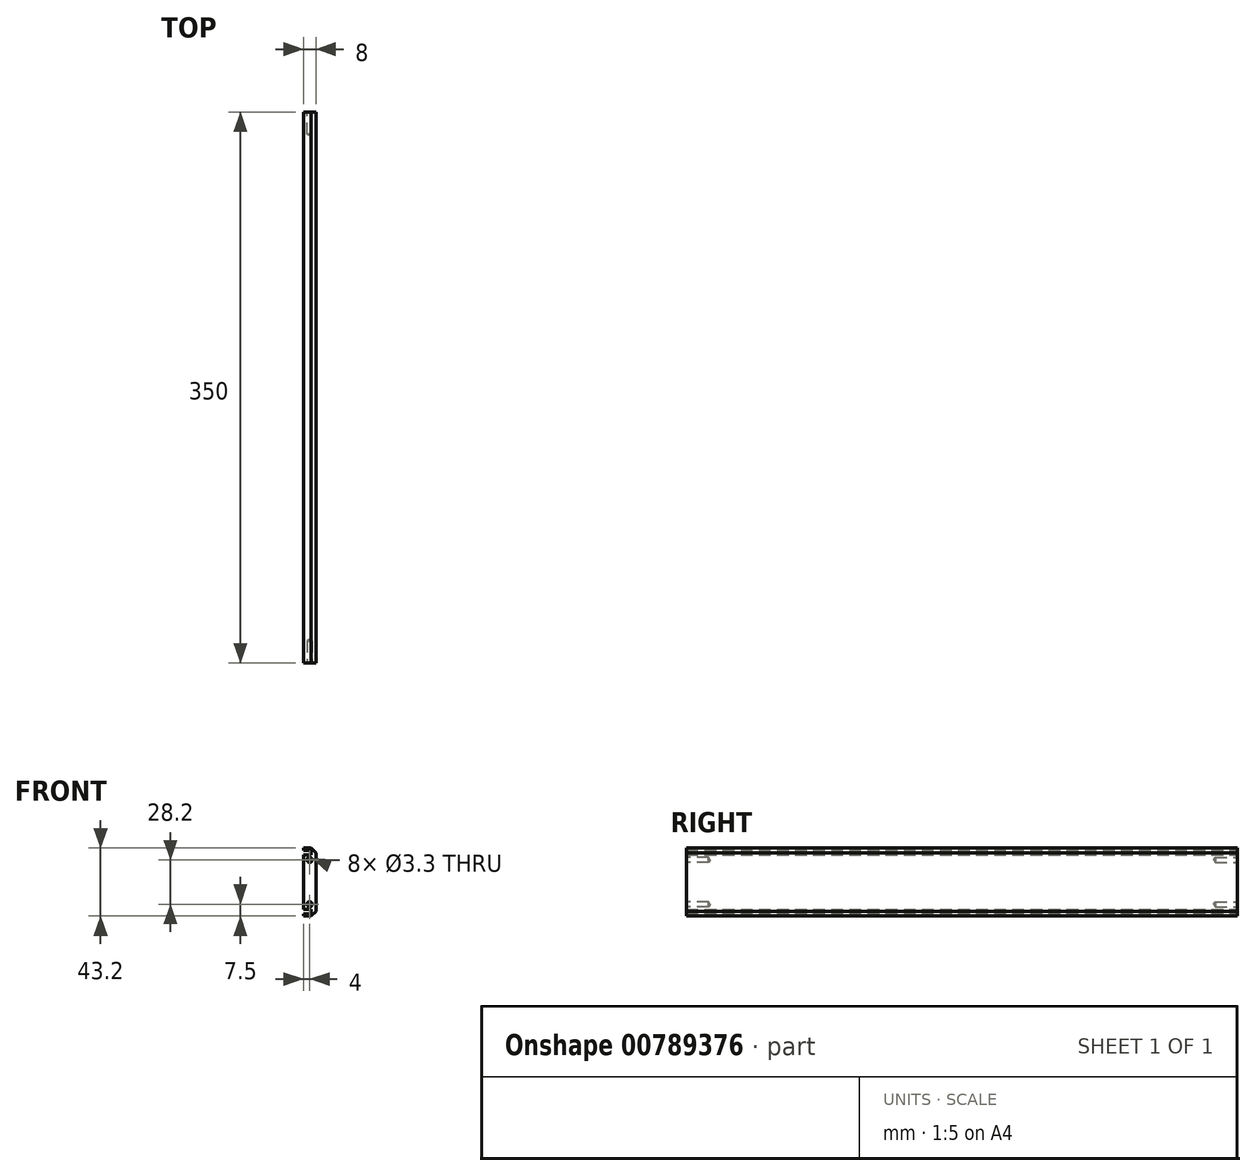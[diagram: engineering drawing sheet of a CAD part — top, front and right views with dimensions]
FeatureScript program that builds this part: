
annotation { "Feature Type Name" : "Feature", "Feature Type Description" : "" }
export const myFeature = defineFeature(function(context is Context, id is Id, definition is map)
    precondition{}
    {
        {
            var Q0;
            Q0=qCreatedBy(makeId("Front.planeOp"),FACE);
            var sketch = newSketch(context, id + "F0", { "sketchPlane" : qUnion([Q0])});
            skLineSegment(sketch, "E0", {"start": v(0, 29.5) * mm, "end": v(5, 29.5) * mm});
            skLineSegment(sketch, "E1", {"start": v(5, 29.5) * mm, "end": v(5, 32.5) * mm});
            skLineSegment(sketch, "E2", {"start": v(5, 32.5) * mm, "end": v(0, 32.5) * mm});
            skLineSegment(sketch, "E3", {"start": v(0, 32.5) * mm, "end": v(0, 33.85) * mm});
            skLineSegment(sketch, "E4", {"start": v(0, 33.85) * mm, "end": v(8, 33.85) * mm});
            skLineSegment(sketch, "E5", {"start": v(8, 33.85) * mm, "end": v(8, -9.35) * mm});
            skLineSegment(sketch, "E6", {"start": v(8, -9.35) * mm, "end": v(0, -9.35) * mm});
            skLineSegment(sketch, "E7", {"start": v(0, -9.35) * mm, "end": v(0, -8) * mm});
            skLineSegment(sketch, "E8", {"start": v(0, -8) * mm, "end": v(5, -8) * mm});
            skLineSegment(sketch, "E9", {"start": v(5, -8) * mm, "end": v(5, -5) * mm});
            skLineSegment(sketch, "E10", {"start": v(5, -5) * mm, "end": v(0, -5) * mm});
            skLineSegment(sketch, "E11", {"start": v(0, -5) * mm, "end": v(0, 29.5) * mm});
            skSolve(sketch);
        }
        {
            var Q0;
            Q0 = qSketchRegion(id + "F0", true);
            extrude(context, id + "F1", {"entities" : qUnion([Q0]), "depth" : 350 * mm, "offsetDistance" : 25 * mm});
        }
        {
            var Q0;
            Q0=makeQuery(id+"F1.opExtrude","SWEPT_EDGE",EDGE,{"disambiguationData":[OSD([sQuery(id+"F0.wireOp",EDGE,"E4"),sQuery(id+"F0.wireOp",EDGE,"E5")])]});
            var Q1;
            Q1=makeQuery(id+"F1.opExtrude","SWEPT_EDGE",EDGE,{"disambiguationData":[OSD([sQuery(id+"F0.wireOp",EDGE,"E5"),sQuery(id+"F0.wireOp",EDGE,"E6")])]});
            chamfer(context, id + "F2", {"entities" : qUnion([Q0, Q1]), "width" : 3 * mm, "tangentPropagation" : true});
        }
        {
            var Q0;
            Q0=makeQuery(id+"F1.opExtrude","CAP_FACE",FACE,{"disambiguationData":[OSD([sQuery(id+"F0.wireOp",EDGE,"E0"),sQuery(id+"F0.wireOp",EDGE,"E1"),sQuery(id+"F0.wireOp",EDGE,"E2"),sQuery(id+"F0.wireOp",EDGE,"E3"),sQuery(id+"F0.wireOp",EDGE,"E4"),sQuery(id+"F0.wireOp",EDGE,"E5"),sQuery(id+"F0.wireOp",EDGE,"E6"),sQuery(id+"F0.wireOp",EDGE,"E7"),sQuery(id+"F0.wireOp",EDGE,"E8"),sQuery(id+"F0.wireOp",EDGE,"E9"),sQuery(id+"F0.wireOp",EDGE,"E10"),sQuery(id+"F0.wireOp",EDGE,"E11")])],"isStart":false});
            var sketch = newSketch(context, id + "F3", { "sketchPlane" : qUnion([Q0])});
            skPoint(sketch, "E12", {"position": v(4, 26.35) * mm});
            skPoint(sketch, "E13", {"position": v(4, -1.85) * mm});
            skSolve(sketch);
        }
        {
            var Q0;
            Q0=sQuery(id+"F3.wireOp",VERTEX,"E12");
            var Q1;
            Q1=sQuery(id+"F3.wireOp",VERTEX,"E13");
            var Q2;
            Q2=makeQuery(id+"F1.opExtrude","SWEPT_BODY",BODY,{"disambiguationData":[OSD([sQuery(id+"F0.wireOp",EDGE,"E0"),sQuery(id+"F0.wireOp",EDGE,"E1"),sQuery(id+"F0.wireOp",EDGE,"E2"),sQuery(id+"F0.wireOp",EDGE,"E3"),sQuery(id+"F0.wireOp",EDGE,"E4"),sQuery(id+"F0.wireOp",EDGE,"E5"),sQuery(id+"F0.wireOp",EDGE,"E6"),sQuery(id+"F0.wireOp",EDGE,"E7"),sQuery(id+"F0.wireOp",EDGE,"E8"),sQuery(id+"F0.wireOp",EDGE,"E9"),sQuery(id+"F0.wireOp",EDGE,"E10"),sQuery(id+"F0.wireOp",EDGE,"E11")])]});
            hole(context, id + "F4", {"style" : HoleStyle.SIMPLE, "endStyle" : HoleEndStyle.BLIND, "standardTappedOrClearance" : lookupTablePath({ "standard" : "ISO", "engagement" : "75%", "pitch" : "0.7 mm", "size" : "M4", "type" : "Tapped" }), "standardBlindInLast" : lookupTablePath({ "standard" : "ISO", "engagement" : "75%", "pitch" : "0.7 mm", "size" : "M4", "type" : "Tapped" }), "holeDiameter" : 3.3 * mm, "majorDiameter" : 4 * mm, "showTappedDepth" : true, "holeDepth" : 14.1 * mm, "isTappedThrough" : true, "tappedDepth" : 12 * mm, "tapClearance" : 3, "locations" : qUnion([Q0, Q1]), "scope" : qUnion([Q2])});
        }
        {
            var Q0;
            Q0=makeQuery(id+"F1.opExtrude","CAP_FACE",FACE,{"disambiguationData":[OSD([sQuery(id+"F0.wireOp",EDGE,"E0"),sQuery(id+"F0.wireOp",EDGE,"E1"),sQuery(id+"F0.wireOp",EDGE,"E2"),sQuery(id+"F0.wireOp",EDGE,"E3"),sQuery(id+"F0.wireOp",EDGE,"E4"),sQuery(id+"F0.wireOp",EDGE,"E5"),sQuery(id+"F0.wireOp",EDGE,"E6"),sQuery(id+"F0.wireOp",EDGE,"E7"),sQuery(id+"F0.wireOp",EDGE,"E8"),sQuery(id+"F0.wireOp",EDGE,"E9"),sQuery(id+"F0.wireOp",EDGE,"E10"),sQuery(id+"F0.wireOp",EDGE,"E11")])],"isStart":true});
            var sketch = newSketch(context, id + "F5", { "sketchPlane" : qUnion([Q0])});
            skPoint(sketch, "E14", {"position": v(-4, 26.35) * mm});
            skPoint(sketch, "E15", {"position": v(-4, -1.85) * mm});
            skSolve(sketch);
        }
        {
            var Q0;
            Q0=sQuery(id+"F5.wireOp",VERTEX,"E14");
            var Q1;
            Q1=sQuery(id+"F5.wireOp",VERTEX,"E15");
            var Q2;
            Q2=makeQuery(id+"F1.opExtrude","SWEPT_BODY",BODY,{"disambiguationData":[OSD([sQuery(id+"F0.wireOp",EDGE,"E0"),sQuery(id+"F0.wireOp",EDGE,"E1"),sQuery(id+"F0.wireOp",EDGE,"E2"),sQuery(id+"F0.wireOp",EDGE,"E3"),sQuery(id+"F0.wireOp",EDGE,"E4"),sQuery(id+"F0.wireOp",EDGE,"E5"),sQuery(id+"F0.wireOp",EDGE,"E6"),sQuery(id+"F0.wireOp",EDGE,"E7"),sQuery(id+"F0.wireOp",EDGE,"E8"),sQuery(id+"F0.wireOp",EDGE,"E9"),sQuery(id+"F0.wireOp",EDGE,"E10"),sQuery(id+"F0.wireOp",EDGE,"E11")])]});
            hole(context, id + "F6", {"style" : HoleStyle.SIMPLE, "endStyle" : HoleEndStyle.BLIND, "standardTappedOrClearance" : lookupTablePath({ "standard" : "ISO", "engagement" : "75%", "pitch" : "0.7 mm", "size" : "M4", "type" : "Tapped" }), "standardBlindInLast" : lookupTablePath({ "standard" : "ISO", "engagement" : "75%", "pitch" : "0.7 mm", "size" : "M4", "type" : "Tapped" }), "holeDiameter" : 3.3 * mm, "majorDiameter" : 4 * mm, "showTappedDepth" : true, "holeDepth" : 14.1 * mm, "isTappedThrough" : true, "tappedDepth" : 12 * mm, "tapClearance" : 3, "locations" : qUnion([Q0, Q1]), "scope" : qUnion([Q2])});
        }
        {
            var Q0;
            Q0=makeQuery(id+"F1.opExtrude","SWEPT_BODY",BODY,{"disambiguationData":[OSD([sQuery(id+"F0.wireOp",EDGE,"E0"),sQuery(id+"F0.wireOp",EDGE,"E1"),sQuery(id+"F0.wireOp",EDGE,"E2"),sQuery(id+"F0.wireOp",EDGE,"E3"),sQuery(id+"F0.wireOp",EDGE,"E4"),sQuery(id+"F0.wireOp",EDGE,"E5"),sQuery(id+"F0.wireOp",EDGE,"E6"),sQuery(id+"F0.wireOp",EDGE,"E7"),sQuery(id+"F0.wireOp",EDGE,"E8"),sQuery(id+"F0.wireOp",EDGE,"E9"),sQuery(id+"F0.wireOp",EDGE,"E10"),sQuery(id+"F0.wireOp",EDGE,"E11")])]});
            transform(context, id + "F7", {"entities" : qUnion([Q0]), "transformType" : TransformType.TRANSLATION_3D, "dx" : 0 * mm, "dy" : 0 * mm, "dz" : 0 * mm, "makeCopy" : true});
        }
    });
